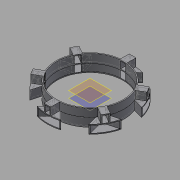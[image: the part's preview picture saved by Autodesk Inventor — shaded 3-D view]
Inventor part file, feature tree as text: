
AUTODESK INVENTOR PART (.ipt)
format: ipt  version: 2015 (Build 190159000, 159)  size: 484,864 bytes
history: native  units: mm
features: sketch x5, extrude x5, plane x2
ambient origin geometry x8: Origin, YZ Plane, XZ Plane, XY Plane, X Axis, Y Axis, Z Axis, Center Point
bodies: Body1 (feature_tree)
feature tree (12):
  sketch  "Sketch1"  dims[d19=68.0mm d22=12.0mm d32=60.0mm d34=360.0deg]
  plane  "Work Plane2"
  plane  "Work Plane1"
  extrude  "Extrusion5"  Depth=60.0mm TaperAngle=360.0deg
  extrude  "Extrusion6"  Depth=7.0mm TaperAngle=0.0deg
  extrude  "Extrusion7"  Depth=35.000142mm
  extrude  "Extrusion8"  Depth=1.0mm TaperAngle=0.0deg
  extrude  "Extrusion9"  Depth=7.0mm TaperAngle=0.0deg
  sketch  "Sketch6"  dims[d36=1.0mm d43=7.0mm d44=0.0mm]
  sketch  "Sketch9"  dims[d48=1.0mm d49=0.0mm d53=35.000142mm]
  sketch  "Sketch10"  dims[d54=34.0mm d55=1.0mm d56=0.0mm]
  sketch  "Sketch11"  dims[d62=60.0mm d64=360.0deg d66=7.0mm d67=0.0mm d69=1.0mm d70=0.0mm]
